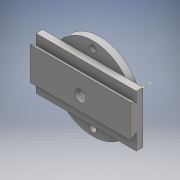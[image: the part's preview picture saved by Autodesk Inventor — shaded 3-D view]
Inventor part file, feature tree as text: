
AUTODESK INVENTOR PART (.ipt)
format: ipt  version: 2016 (Build 200138000, 138)  size: 150,528 bytes
history: native  units: mm
features: sketch x8, extrude x6
ambient origin geometry x8: Origin, YZ Plane, XZ Plane, XY Plane, X Axis, Y Axis, Z Axis, Center Point
bodies: Solid1 (feature_tree)
feature tree (14):
  extrude  "Extrusion1"  Depth=85.6mm
  sketch  "Sketch2"  dims[d5=20.3mm d6=54.5mm]
  extrude  "Extrusion2"  Depth=54.5mm
  extrude  "Extrusion3"  Depth=165.2mm TaperAngle=0.0deg
  extrude  "Extrusion4"  Depth=68.3mm
  sketch  "Sketch6"  dims[d15=73.75mm d16=0.0mm d17=6.0mm]
  extrude  "Extrusion5"  Depth=11.5mm
  extrude  "Extrusion6"  Depth=6.0mm
  sketch  "Sketch1"  dims[d1=85.6mm d2=26.6mm]
  sketch  "Sketch3"  dims[d7=17.0mm d8=165.2mm d9=0.0mm]
  sketch  "Sketch4"  dims[d10=14.0mm d11=68.3mm]
  sketch  "Sketch5"  dims[d12=11.5mm d13=0.0mm d14=18.3mm]
  sketch  "Sketch7"  dims[d18=6.0mm]
  sketch  "Sketch8"  dims[d19=5.4mm d20=5.4mm d21=73.75mm d22=0.0mm d23=6.9mm d24=10.8mm d25=6.0mm d26=0.0mm d27=6.2mm d28=22.8mm d29=0.0mm]
